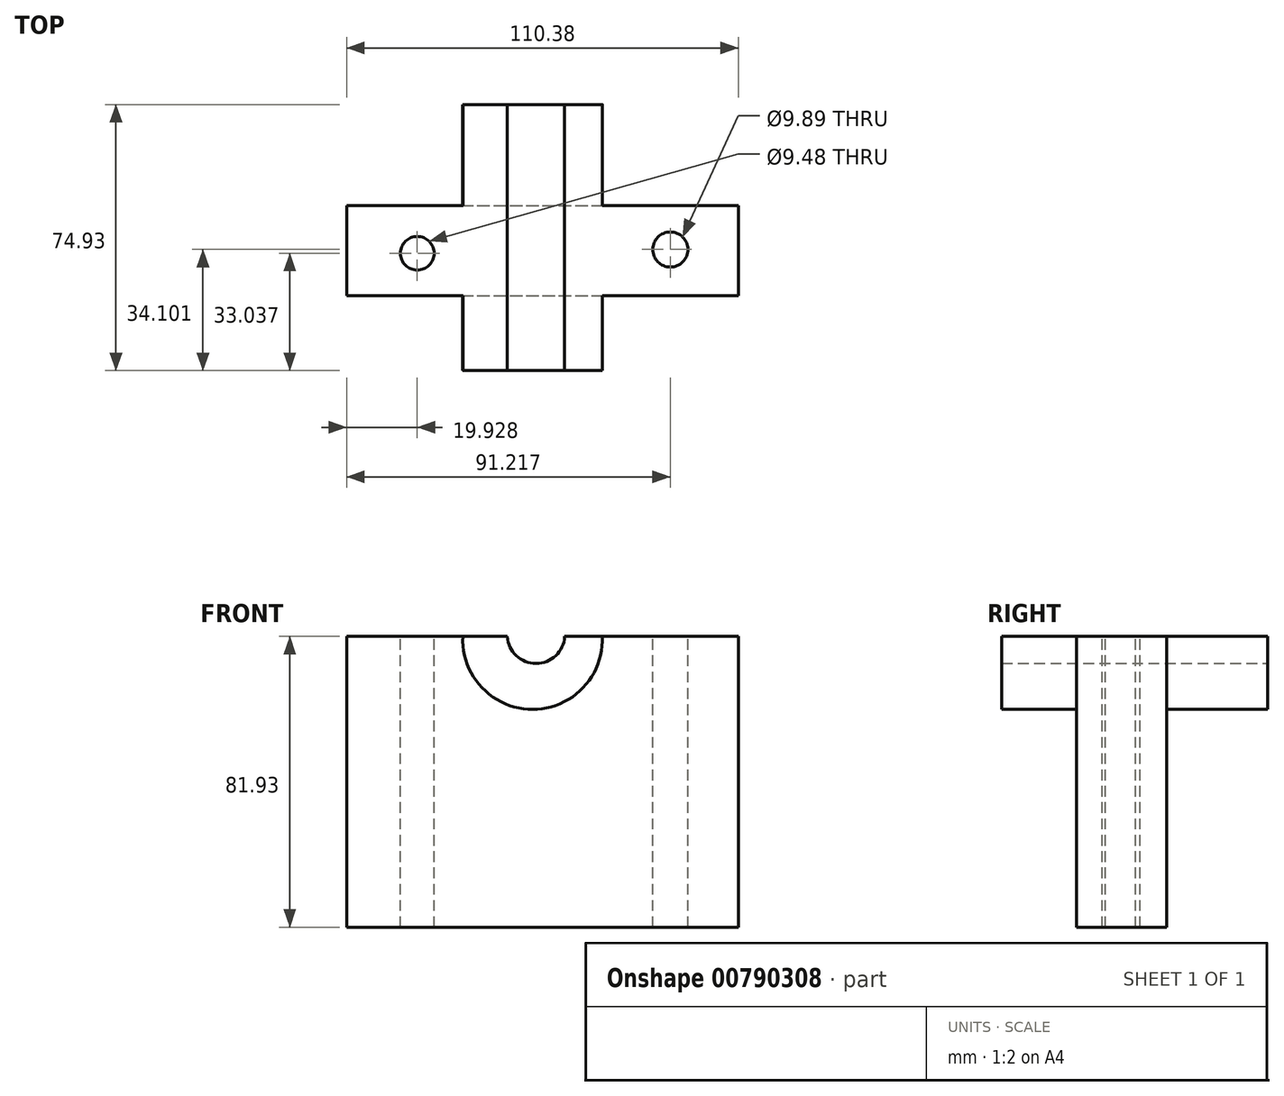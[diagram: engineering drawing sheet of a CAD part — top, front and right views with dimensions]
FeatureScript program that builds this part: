
annotation { "Feature Type Name" : "Feature", "Feature Type Description" : "" }
export const myFeature = defineFeature(function(context is Context, id is Id, definition is map)
    precondition{}
    {
        {
            var Q0;
            Q0=qCreatedBy(makeId("Front.planeOp"),FACE);
            var sketch = newSketch(context, id + "F0", { "sketchPlane" : qUnion([Q0])});
            skLineSegment(sketch, "E0.bottom", {"start": v(-53.14, 37.47) * mm, "end": v(57.24, 37.47) * mm});
            skLineSegment(sketch, "E0.top", {"start": v(-53.14, -44.46) * mm, "end": v(57.24, -44.46) * mm});
            skLineSegment(sketch, "E0.left", {"start": v(-53.14, 37.47) * mm, "end": v(-53.14, -44.46) * mm});
            skLineSegment(sketch, "E0.right", {"start": v(57.24, 37.47) * mm, "end": v(57.24, -44.46) * mm});
            skArc(sketch, "E1", {"start": v(-7.83, 37.47) * mm, "mid": v(0.24, 29.85) * mm, "end": v(8.31, 37.47) * mm});
            skArc(sketch, "E2", {"start": v(-20.36, 37.47) * mm, "mid": v(-0.72, 16.93) * mm, "end": v(18.92, 37.47) * mm});
            skSolve(sketch);
        }
        {
            var Q0;
            Q0=makeQuery(id+"F0.imprint","IMPRINT",FACE,{"disambiguationData":[TD([[makeQuery(id+"F0.imprint","IMPRINT",EDGE,{"derivedFrom":sQuery(id+"F0.wireOp",EDGE,"E0.top")}),1.0]])]});
            extrude(context, id + "F1", {"entities" : qUnion([Q0]), "depth" : 25.4 * mm, "offsetDistance" : 25.4 * mm});
        }
        {
            var Q0;
            {var subQ0=sQuery(id+"F0.wireOp",EDGE,"E1");Q0=makeQuery(id+"F0.imprint","IMPRINT",FACE,{"disambiguationData":[TD([[makeQuery(id+"F0.imprint","IMPRINT",EDGE,{"derivedFrom":subQ0}),-1.0]])]});}
            extrude(context, id + "F2", {"entities" : qUnion([Q0]), "operationType" : NewBodyOperationType.ADD, "depth" : 46.48 * mm, "offsetDistance" : 25.4 * mm});
        }
        {
            var Q0;
            {var subQ0=sQuery(id+"F0.wireOp",EDGE,"E1");Q0=makeQuery(id+"F0.imprint","IMPRINT",FACE,{"disambiguationData":[TD([[makeQuery(id+"F0.imprint","IMPRINT",EDGE,{"derivedFrom":subQ0}),-1.0]])]});}
            extrude(context, id + "F3", {"entities" : qUnion([Q0]), "operationType" : NewBodyOperationType.ADD, "oppositeDirection" : true, "depth" : 28.45 * mm, "offsetDistance" : 25.4 * mm});
        }
        {
            var Q0;
            {var subQ0=sQuery(id+"F0.wireOp",EDGE,"E0.bottom");var subQ2=makeQuery(id+"F0.imprint","IMPRINT",EDGE,{"disambiguationData":[TD([[makeQuery(id+"F0.imprint","INTERSECT",VERTEX,{"disambiguationData":[OD(1.0)],"derivedFrom":[subQ0,sQuery(id+"F0.wireOp",EDGE,"E1")]}),-1.0]])],"derivedFrom":subQ0});Q0=makeQuery(id+"F3.boolean.opBoolean","MERGE",FACE,{"derivedFrom":[makeQuery(id+"F2.boolean.opBoolean","MERGE",FACE,{"derivedFrom":[makeQuery(id+"F1.opExtrude","SWEPT_FACE",FACE,{"disambiguationData":[OSD([subQ0]),TDD([makeQuery(id+"F0.imprint","IMPRINT",EDGE,{"disambiguationData":[TD([[makeQuery(id+"F0.imprint","INTERSECT",VERTEX,{"derivedFrom":[subQ0,sQuery(id+"F0.wireOp",EDGE,"E0.right")]}),1.0]])],"derivedFrom":subQ0})])]}),makeQuery(id+"F2.opExtrude","SWEPT_FACE",FACE,{"disambiguationData":[OSD([subQ0]),TDD([subQ2])]})]}),makeQuery(id+"F3.opExtrude","SWEPT_FACE",FACE,{"disambiguationData":[OSD([subQ0]),TDD([subQ2])]})]});}
            var sketch = newSketch(context, id + "F4", { "sketchPlane" : qUnion([Q0])});
            skCircle(sketch, "E3", {"center": v(38.08, -12.38) * mm, "radius": 4.94 * mm});
            skPoint(sketch, "E3.centerSnap0", {"position": v(38.08, 0) * mm});
            skSolve(sketch);
        }
        {
            var Q0;
            Q0=makeQuery(id+"F4.imprint","IMPRINT",FACE,{"disambiguationData":[TD([[makeQuery(id+"F4.imprint","IMPRINT",EDGE,{"derivedFrom":sQuery(id+"F4.wireOp",EDGE,"E3")}),1.0]])]});
            extrude(context, id + "F5", {"entities" : qUnion([Q0]), "operationType" : NewBodyOperationType.REMOVE, "oppositeDirection" : true, "depth" : 146.3 * mm, "offsetDistance" : 25.4 * mm});
        }
        {
            var Q0;
            {var subQ0=sQuery(id+"F0.wireOp",EDGE,"E0.bottom");var subQ2=makeQuery(id+"F0.imprint","IMPRINT",EDGE,{"disambiguationData":[TD([[makeQuery(id+"F0.imprint","INTERSECT",VERTEX,{"disambiguationData":[OD(0.0)],"derivedFrom":[subQ0,sQuery(id+"F0.wireOp",EDGE,"E1")]}),1.0]])],"derivedFrom":subQ0});Q0=makeQuery(id+"F3.boolean.opBoolean","MERGE",FACE,{"derivedFrom":[makeQuery(id+"F2.boolean.opBoolean","MERGE",FACE,{"derivedFrom":[makeQuery(id+"F1.opExtrude","SWEPT_FACE",FACE,{"disambiguationData":[OSD([subQ0]),TDD([makeQuery(id+"F0.imprint","IMPRINT",EDGE,{"disambiguationData":[TD([[makeQuery(id+"F0.imprint","INTERSECT",VERTEX,{"derivedFrom":[subQ0,sQuery(id+"F0.wireOp",EDGE,"E0.left")]}),-1.0]])],"derivedFrom":subQ0})])]}),makeQuery(id+"F2.opExtrude","SWEPT_FACE",FACE,{"disambiguationData":[OSD([subQ0]),TDD([subQ2])]})]}),makeQuery(id+"F3.opExtrude","SWEPT_FACE",FACE,{"disambiguationData":[OSD([subQ0]),TDD([subQ2])]})]});}
            var sketch = newSketch(context, id + "F6", { "sketchPlane" : qUnion([Q0])});
            skCircle(sketch, "E4", {"center": v(-33.21, -13.44) * mm, "radius": 4.74 * mm});
            skSolve(sketch);
        }
        {
            var Q0;
            Q0=makeQuery(id+"F6.imprint","IMPRINT",FACE,{"disambiguationData":[TD([[makeQuery(id+"F6.imprint","IMPRINT",EDGE,{"derivedFrom":sQuery(id+"F6.wireOp",EDGE,"E4")}),1.0]])]});
            extrude(context, id + "F7", {"entities" : qUnion([Q0]), "operationType" : NewBodyOperationType.REMOVE, "oppositeDirection" : true, "depth" : 190.75 * mm, "offsetDistance" : 25.4 * mm});
        }
    });
